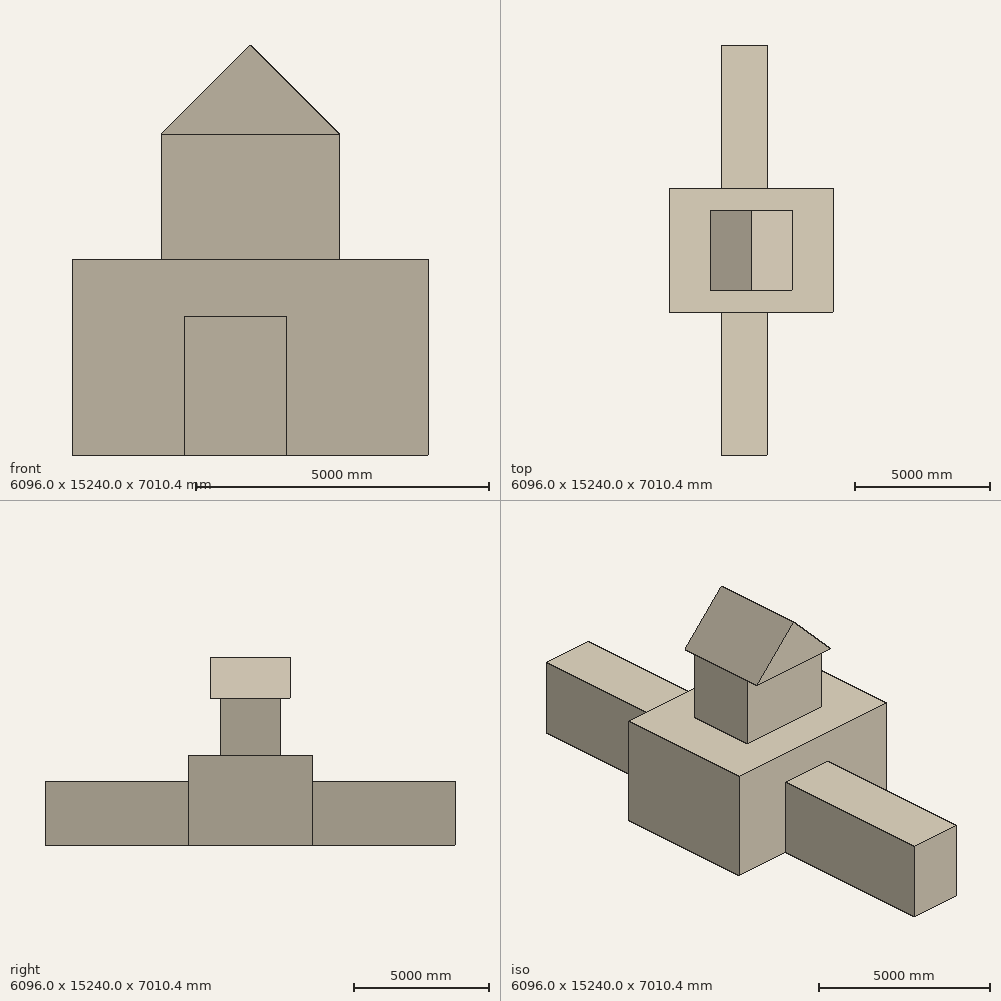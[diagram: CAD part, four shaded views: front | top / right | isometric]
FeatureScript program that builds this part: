
annotation { "Feature Type Name" : "Feature", "Feature Type Description" : "" }
export const myFeature = defineFeature(function(context is Context, id is Id, definition is map)
    precondition{}
    {
        {
            var Q0;
            Q0=qCreatedBy(makeId("Front.planeOp"),FACE);
            var sketch = newSketch(context, id + "F0", { "sketchPlane" : qUnion([Q0])});
            skLineSegment(sketch, "E0", {"start": v(0, 0) * mm, "end": v(-1524, 0) * mm});
            skLineSegment(sketch, "E1", {"start": v(0, 0) * mm, "end": v(1524, 0) * mm});
            skLineSegment(sketch, "E2", {"start": v(0, 0) * mm, "end": v(0, 1524) * mm});
            skLineSegment(sketch, "E3", {"start": v(-1524, 0) * mm, "end": v(0, 1524) * mm});
            skLineSegment(sketch, "E4", {"start": v(0, 1524) * mm, "end": v(1524, 0) * mm});
            skLineSegment(sketch, "E5", {"start": v(-1524, 0) * mm, "end": v(-1524, -2133.6) * mm});
            skLineSegment(sketch, "E6", {"start": v(-1524, -2133.6) * mm, "end": v(1524, -2133.6) * mm});
            skLineSegment(sketch, "E7", {"start": v(-1524, -2133.6) * mm, "end": v(-3048, -2133.6) * mm});
            skLineSegment(sketch, "E8", {"start": v(1524, -2133.6) * mm, "end": v(3048, -2133.6) * mm});
            skLineSegment(sketch, "E9", {"start": v(-3048, -2133.6) * mm, "end": v(-3048, -5486.4) * mm});
            skLineSegment(sketch, "E10", {"start": v(3048, -2133.6) * mm, "end": v(3048, -5486.4) * mm});
            skLineSegment(sketch, "E11", {"start": v(-3048, -5486.4) * mm, "end": v(3048, -5486.4) * mm});
            skLineSegment(sketch, "E12", {"start": v(-13577.84, 147.9) * mm, "end": v(-13577.84, -156.9) * mm});
            skPoint(sketch, "E13.endSnap0", {"position": v(0, -2133.6) * mm});
            skLineSegment(sketch, "E14", {"start": v(1524, 0) * mm, "end": v(1524, -2133.6) * mm});
            skLineSegment(sketch, "E15", {"start": v(-1127.76, -5486.4) * mm, "end": v(-1127.76, -3108.96) * mm});
            skLineSegment(sketch, "E16", {"start": v(-1127.76, -3108.96) * mm, "end": v(609.6, -3108.96) * mm});
            skLineSegment(sketch, "E17", {"start": v(609.6, -3108.96) * mm, "end": v(609.6, -5486.4) * mm});
            skLineSegment(sketch, "E18", {"start": v(-1127.76, -5486.4) * mm, "end": v(609.6, -5486.4) * mm});
            skSolve(sketch);
        }
        {
            var Q0;
            Q0=makeQuery(id+"F0.imprint","IMPRINT",FACE,{"disambiguationData":[TD([[makeQuery(id+"F0.imprint","IMPRINT",EDGE,{"derivedFrom":sQuery(id+"F0.wireOp",EDGE,"E0")}),-1.0]])]});
            var Q1;
            Q1=makeQuery(id+"F0.imprint","IMPRINT",FACE,{"disambiguationData":[TD([[makeQuery(id+"F0.imprint","IMPRINT",EDGE,{"derivedFrom":sQuery(id+"F0.wireOp",EDGE,"E1")}),1.0]])]});
            extrude(context, id + "F1", {"entities" : qUnion([Q0, Q1]), "endBound" : BoundingType.SYMMETRIC, "depth" : 2987.04 * mm, "offsetDistance" : 30.48 * mm});
        }
        {
            var Q0;
            Q0=makeQuery(id+"F0.imprint","IMPRINT",FACE,{"disambiguationData":[TD([[makeQuery(id+"F0.imprint","IMPRINT",EDGE,{"derivedFrom":sQuery(id+"F0.wireOp",EDGE,"E0")}),1.0]])]});
            extrude(context, id + "F2", {"entities" : qUnion([Q0]), "operationType" : NewBodyOperationType.ADD, "endBound" : BoundingType.SYMMETRIC, "depth" : 2194.56 * mm, "offsetDistance" : 30.48 * mm});
        }
        {
            var Q0;
            Q0=makeQuery(id+"F0.imprint","IMPRINT",FACE,{"disambiguationData":[TD([[makeQuery(id+"F0.imprint","IMPRINT",EDGE,{"derivedFrom":sQuery(id+"F0.wireOp",EDGE,"E15")}),-1.0]])]});
            extrude(context, id + "F3", {"entities" : qUnion([Q0]), "depth" : 30.48 * mm, "offsetDistance" : 30.48 * mm});
        }
        {
            var Q0;
            Q0=makeQuery(id+"F0.imprint","IMPRINT",FACE,{"disambiguationData":[TD([[makeQuery(id+"F0.imprint","IMPRINT",EDGE,{"derivedFrom":sQuery(id+"F0.wireOp",EDGE,"E15")}),-1.0]])]});
            extrude(context, id + "F4", {"entities" : qUnion([Q0]), "operationType" : NewBodyOperationType.ADD, "endBound" : BoundingType.SYMMETRIC, "depth" : 15240 * mm, "offsetDistance" : 30.48 * mm});
        }
        {
            var Q0;
            Q0=makeQuery(id+"F0.imprint","IMPRINT",FACE,{"disambiguationData":[TD([[makeQuery(id+"F0.imprint","IMPRINT",EDGE,{"derivedFrom":sQuery(id+"F0.wireOp",EDGE,"E6")}),-1.0]])]});
            extrude(context, id + "F5", {"entities" : qUnion([Q0]), "endBound" : BoundingType.SYMMETRIC, "depth" : 4572 * mm, "offsetDistance" : 30.48 * mm});
        }
    });
